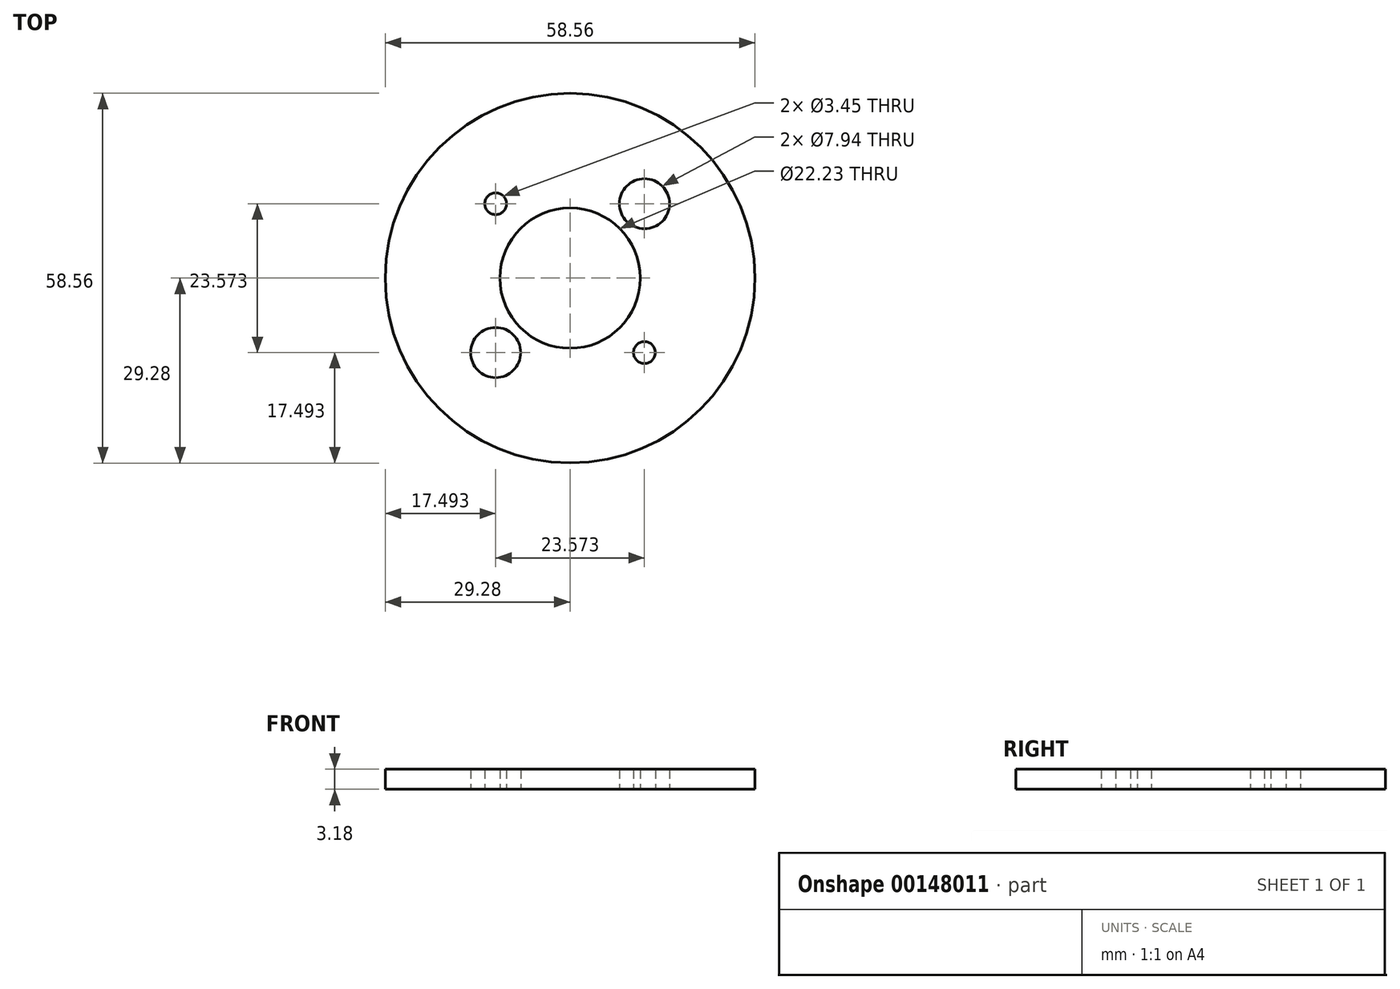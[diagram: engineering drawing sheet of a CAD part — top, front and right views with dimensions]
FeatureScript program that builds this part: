
annotation { "Feature Type Name" : "Feature", "Feature Type Description" : "" }
export const myFeature = defineFeature(function(context is Context, id is Id, definition is map)
    precondition{}
    {
        {
            var Q0;
            Q0=qCreatedBy(makeId("Top.planeOp"),FACE);
            var sketch = newSketch(context, id + "F0", { "sketchPlane" : qUnion([Q0])});
            skCircle(sketch, "E0", {"center": v(0, 0) * mm, "radius": 29.28 * mm});
            skCircle(sketch, "E1", {"center": v(0, 0) * mm, "radius": 11.11 * mm});
            skLineSegment(sketch, "E2.bottom", {"start": v(-11.79, 11.79) * mm, "end": v(11.79, 11.79) * mm, "construction": true});
            skLineSegment(sketch, "E2.top", {"start": v(-11.79, -11.79) * mm, "end": v(11.79, -11.79) * mm, "construction": true});
            skLineSegment(sketch, "E2.left", {"start": v(-11.79, 11.79) * mm, "end": v(-11.79, -11.79) * mm, "construction": true});
            skLineSegment(sketch, "E2.right", {"start": v(11.79, 11.79) * mm, "end": v(11.79, -11.79) * mm, "construction": true});
            skCircle(sketch, "E3", {"center": v(11.79, 11.79) * mm, "radius": 1.73 * mm, "construction": true});
            skCircle(sketch, "E4", {"center": v(-11.79, 11.79) * mm, "radius": 1.73 * mm});
            skCircle(sketch, "E5", {"center": v(-11.79, -11.79) * mm, "radius": 1.73 * mm, "construction": true});
            skCircle(sketch, "E6", {"center": v(11.79, -11.79) * mm, "radius": 1.73 * mm});
            skCircle(sketch, "E7", {"center": v(-11.79, -11.79) * mm, "radius": 3.97 * mm});
            skCircle(sketch, "E8", {"center": v(11.79, 11.79) * mm, "radius": 3.97 * mm});
            skCircle(sketch, "E9", {"center": v(11.79, 11.79) * mm, "radius": 5.56 * mm, "construction": true});
            skSolve(sketch);
        }
        {
            var Q0;
            Q0=qSketchRegion(id+"F0",true);
            extrude(context, id + "F1", {"entities" : qUnion([Q0]), "depth" : 3.17 * mm});
        }
    });
